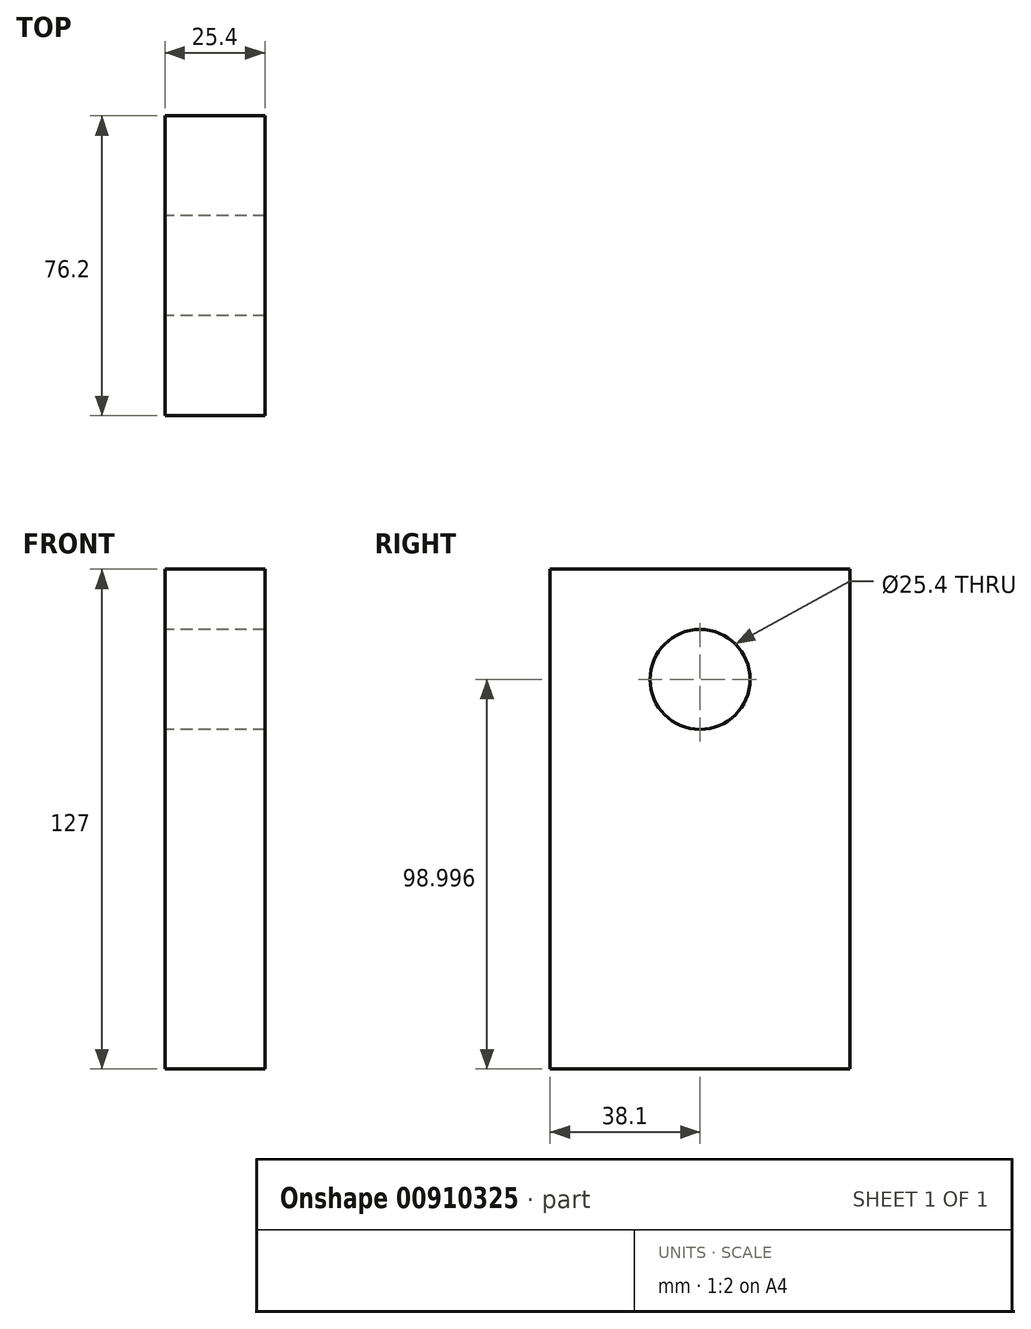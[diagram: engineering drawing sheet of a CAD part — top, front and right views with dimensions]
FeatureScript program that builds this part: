
annotation { "Feature Type Name" : "Feature", "Feature Type Description" : "" }
export const myFeature = defineFeature(function(context is Context, id is Id, definition is map)
    precondition{}
    {
        {
            var Q0;
            Q0=qCreatedBy(makeId("Right.planeOp"),FACE);
            var sketch = newSketch(context, id + "F0", { "sketchPlane" : qUnion([Q0])});
            skLineSegment(sketch, "E0.bottom", {"start": v(-76.2, 67.91) * mm, "end": v(0, 67.91) * mm});
            skLineSegment(sketch, "E0.top", {"start": v(-76.2, -59.09) * mm, "end": v(0, -59.09) * mm});
            skLineSegment(sketch, "E0.left", {"start": v(-76.2, 67.91) * mm, "end": v(-76.2, -59.09) * mm});
            skLineSegment(sketch, "E0.right", {"start": v(0, 67.91) * mm, "end": v(0, -59.09) * mm});
            skSolve(sketch);
        }
        {
            var Q0;
            Q0=makeQuery(id+"F0.imprint","IMPRINT",FACE,{"disambiguationData":[TD([[makeQuery(id+"F0.imprint","IMPRINT",EDGE,{"derivedFrom":sQuery(id+"F0.wireOp",EDGE,"E0.bottom")}),-1.0]])]});
            extrude(context, id + "F1", {"entities" : qUnion([Q0]), "depth" : 25.4 * mm, "offsetDistance" : 25.4 * mm});
        }
        {
            var Q0;
            Q0=makeQuery(id+"F1.opExtrude","CAP_FACE",FACE,{"disambiguationData":[OSD([sQuery(id+"F0.wireOp",EDGE,"E0.bottom"),sQuery(id+"F0.wireOp",EDGE,"E0.top"),sQuery(id+"F0.wireOp",EDGE,"E0.left"),sQuery(id+"F0.wireOp",EDGE,"E0.right")])],"isStart":true});
            var sketch = newSketch(context, id + "F2", { "sketchPlane" : qUnion([Q0])});
            skCircle(sketch, "E1", {"center": v(38.1, 39.9) * mm, "radius": 12.7 * mm});
            skSolve(sketch);
        }
        {
            var Q0;
            Q0=makeQuery(id+"F2.imprint","IMPRINT",FACE,{"disambiguationData":[TD([[makeQuery(id+"F2.imprint","IMPRINT",EDGE,{"derivedFrom":sQuery(id+"F2.wireOp",EDGE,"E1")}),1.0]])]});
            extrude(context, id + "F3", {"entities" : qUnion([Q0]), "operationType" : NewBodyOperationType.REMOVE, "endBound" : BoundingType.THROUGH_ALL, "oppositeDirection" : true, "depth" : 25.4 * mm, "offsetDistance" : 25.4 * mm});
        }
    });
